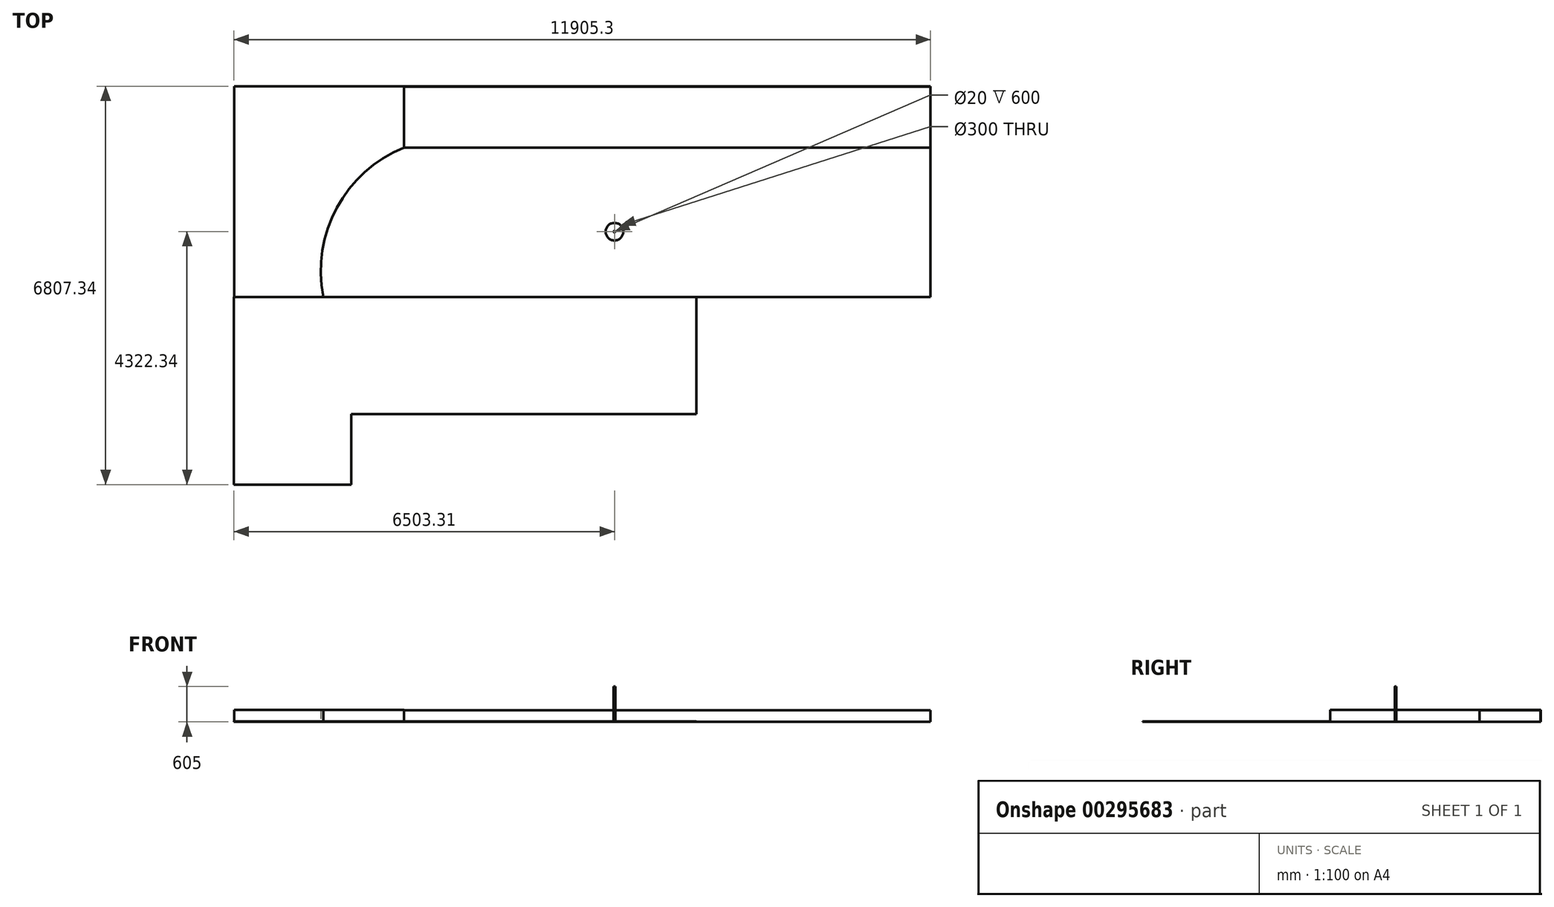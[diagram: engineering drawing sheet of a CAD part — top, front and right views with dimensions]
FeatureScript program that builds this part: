
annotation { "Feature Type Name" : "Feature", "Feature Type Description" : "" }
export const myFeature = defineFeature(function(context is Context, id is Id, definition is map)
    precondition{}
    {
        {
            var Q0;
            Q0=qCreatedBy(makeId("Top.planeOp"),FACE);
            var sketch = newSketch(context, id + "F0", { "sketchPlane" : qUnion([Q0])});
            skLineSegment(sketch, "E0", {"start": v(0, 0) * mm, "end": v(0, 3600) * mm});
            skLineSegment(sketch, "E1", {"start": v(0, 3600) * mm, "end": v(-11900, 3600) * mm});
            skLineSegment(sketch, "E2", {"start": v(-11900, 3600) * mm, "end": v(-11900, -3200) * mm});
            skLineSegment(sketch, "E3", {"start": v(-11900, -3200) * mm, "end": v(-9900, -3200) * mm});
            skLineSegment(sketch, "E4", {"start": v(-9900, -3200) * mm, "end": v(-9900, -2000) * mm});
            skLineSegment(sketch, "E5", {"start": v(-9900, -2000) * mm, "end": v(-9900, 0) * mm});
            skLineSegment(sketch, "E6", {"start": v(-9900, 0) * mm, "end": v(0, 0) * mm});
            skLineSegment(sketch, "E7", {"start": v(-9900, -2000) * mm, "end": v(-4000, -2000) * mm});
            skLineSegment(sketch, "E8", {"start": v(-4000, -2000) * mm, "end": v(-4000, 0) * mm});
            skSolve(sketch);
        }
        {
            var Q0;
            {var subQ0=sQuery(id+"F0.wireOp",EDGE,"E0");Q0=makeQuery(id+"F0.imprint","IMPRINT",FACE,{"disambiguationData":[TD([[makeQuery(id+"F0.imprint","IMPRINT",EDGE,{"derivedFrom":subQ0}),1.0]])]});}
            extrude(context, id + "F1", {"entities" : qUnion([Q0]), "depth" : 5 * mm});
        }
        {
            var Q0;
            Q0=qCreatedBy(makeId("Top.planeOp"),FACE);
            var sketch = newSketch(context, id + "F2", { "sketchPlane" : qUnion([Q0])});
            skLineSegment(sketch, "E9.bottom", {"start": v(-9902, 0) * mm, "end": v(-4002, 0) * mm});
            skLineSegment(sketch, "E9.top", {"start": v(-9902, -2000) * mm, "end": v(-4002, -2000) * mm});
            skLineSegment(sketch, "E9.right", {"start": v(-4002, 0) * mm, "end": v(-4002, -2000) * mm});
            skLineSegment(sketch, "E10", {"start": v(-9902, 0) * mm, "end": v(-11905.3, 0) * mm});
            skLineSegment(sketch, "E11", {"start": v(-11905.3, 0) * mm, "end": v(-11905.3, -3207.34) * mm});
            skLineSegment(sketch, "E12", {"start": v(-11905.3, -3207.34) * mm, "end": v(-9902, -3207.34) * mm});
            skLineSegment(sketch, "E13", {"start": v(-9902, -3207.34) * mm, "end": v(-9902, -2000) * mm});
            skSolve(sketch);
        }
        {
            var Q0;
            Q0 = qSketchRegion(id + "F2", true);
            extrude(context, id + "F3", {"entities" : qUnion([Q0]), "operationType" : NewBodyOperationType.ADD, "depth" : 10 * mm});
        }
        {
            var Q0;
            Q0=qCreatedBy(makeId("Top.planeOp"),FACE);
            var sketch = newSketch(context, id + "F4", { "sketchPlane" : qUnion([Q0])});
            skLineSegment(sketch, "E14.bottom", {"start": v(0, 3592.64) * mm, "end": v(-9000, 3592.64) * mm});
            skLineSegment(sketch, "E14.top", {"start": v(0, 2552.64) * mm, "end": v(-9000, 2552.64) * mm});
            skLineSegment(sketch, "E14.left", {"start": v(0, 3592.64) * mm, "end": v(0, 2552.64) * mm});
            skLineSegment(sketch, "E14.right", {"start": v(-9000, 3592.64) * mm, "end": v(-9000, 2552.64) * mm});
            skSolve(sketch);
        }
        {
            var Q0;
            Q0 = qSketchRegion(id + "F4", true);
            extrude(context, id + "F5", {"entities" : qUnion([Q0]), "operationType" : NewBodyOperationType.ADD, "depth" : 200 * mm});
        }
        {
            var Q0;
            {var subQ0=sQuery(id+"F0.wireOp",EDGE,"E6");var subQ1=sQuery(id+"F0.wireOp",EDGE,"E2");var subQ2=sQuery(id+"F0.wireOp",EDGE,"E1");var subQ3=sQuery(id+"F0.wireOp",EDGE,"E0");Q0=makeQuery(id+"F3.boolean.opBoolean","SPLIT",FACE,{"disambiguationData":[TD([makeQuery(id+"F1.opExtrude","SWEPT_FACE",FACE,{"disambiguationData":[OSD([subQ3])]})])],"derivedFrom":makeQuery(id+"F1.opExtrude","CAP_FACE",FACE,{"disambiguationData":[OSD([subQ3,subQ2,subQ1,sQuery(id+"F0.wireOp",EDGE,"E3"),sQuery(id+"F0.wireOp",EDGE,"E4"),sQuery(id+"F0.wireOp",EDGE,"E5"),subQ0])],"isStart":false})});}
            var sketch = newSketch(context, id + "F6", { "sketchPlane" : qUnion([Q0])});
            skLineSegment(sketch, "E15.bottom", {"start": v(-4002, 0) * mm, "end": v(-5402, 0) * mm});
            skLineSegment(sketch, "E15.top", {"start": v(-4002, 1115) * mm, "end": v(-5402, 1115) * mm});
            skLineSegment(sketch, "E15.left", {"start": v(-4002, 0) * mm, "end": v(-4002, 1115) * mm});
            skLineSegment(sketch, "E15.right", {"start": v(-5402, 0) * mm, "end": v(-5402, 1115) * mm});
            skSolve(sketch);
        }
        {
            var Q0;
            Q0=sQuery(id+"F6.wireOp",VERTEX,"E15.right.end");
            var Q1;
            Q1=makeQuery(id+"F1.opExtrude","SWEPT_BODY",BODY,{"disambiguationData":[OSD([sQuery(id+"F0.wireOp",EDGE,"E0"),sQuery(id+"F0.wireOp",EDGE,"E1"),sQuery(id+"F0.wireOp",EDGE,"E2"),sQuery(id+"F0.wireOp",EDGE,"E3"),sQuery(id+"F0.wireOp",EDGE,"E4"),sQuery(id+"F0.wireOp",EDGE,"E5"),sQuery(id+"F0.wireOp",EDGE,"E6")])]});
            hole(context, id + "F7", {"style" : HoleStyle.SIMPLE, "endStyle" : HoleEndStyle.THROUGH, "holeDiameter" : 300 * mm, "tappedDepth" : 12 * mm, "tapClearance" : 3, "locations" : qUnion([Q0]), "scope" : qUnion([Q1])});
        }
        {
            var Q0;
            {var subQ0=sQuery(id+"F0.wireOp",EDGE,"E6");var subQ1=sQuery(id+"F0.wireOp",EDGE,"E2");var subQ2=sQuery(id+"F0.wireOp",EDGE,"E1");var subQ3=sQuery(id+"F0.wireOp",EDGE,"E0");Q0=makeQuery(id+"F3.boolean.opBoolean","SPLIT",FACE,{"disambiguationData":[TD([makeQuery(id+"F1.opExtrude","SWEPT_FACE",FACE,{"disambiguationData":[OSD([subQ3])]})])],"derivedFrom":makeQuery(id+"F1.opExtrude","CAP_FACE",FACE,{"disambiguationData":[OSD([subQ3,subQ2,subQ1,sQuery(id+"F0.wireOp",EDGE,"E3"),sQuery(id+"F0.wireOp",EDGE,"E4"),sQuery(id+"F0.wireOp",EDGE,"E5"),subQ0])],"isStart":false})});}
            var sketch = newSketch(context, id + "F8", { "sketchPlane" : qUnion([Q0])});
            skLineSegment(sketch, "E16.right", {"start": v(-5402, 0) * mm, "end": v(-5402, 1115) * mm});
            skCircle(sketch, "E17", {"center": v(-5402, 1115) * mm, "radius": 10 * mm});
            skCircle(sketch, "E18", {"center": v(-5402, 1115) * mm, "radius": 15 * mm});
            skSolve(sketch);
        }
        {
            var Q0;
            Q0 = qSketchRegion(id + "F8", true);
            extrude(context, id + "F9", {"entities" : qUnion([Q0]), "depth" : 600 * mm});
        }
        {
            var Q0;
            {var subQ0=sQuery(id+"F0.wireOp",EDGE,"E6");var subQ1=sQuery(id+"F0.wireOp",EDGE,"E2");var subQ2=sQuery(id+"F0.wireOp",EDGE,"E1");var subQ3=sQuery(id+"F0.wireOp",EDGE,"E0");Q0=makeQuery(id+"F3.boolean.opBoolean","SPLIT",FACE,{"disambiguationData":[TD([makeQuery(id+"F1.opExtrude","SWEPT_FACE",FACE,{"disambiguationData":[OSD([subQ3])]})])],"derivedFrom":makeQuery(id+"F1.opExtrude","CAP_FACE",FACE,{"disambiguationData":[OSD([subQ3,subQ2,subQ1,sQuery(id+"F0.wireOp",EDGE,"E3"),sQuery(id+"F0.wireOp",EDGE,"E4"),sQuery(id+"F0.wireOp",EDGE,"E5"),subQ0])],"isStart":false})});}
            var sketch = newSketch(context, id + "F10", { "sketchPlane" : qUnion([Q0])});
            skArc(sketch, "E19", {"start": v(-9000, 2552.64) * mm, "mid": v(-10148.37, 1524.1) * mm, "end": v(-10380.33, 0) * mm});
            skLineSegment(sketch, "E20", {"start": v(-10380.33, 0) * mm, "end": v(-11900, 0) * mm});
            skLineSegment(sketch, "E21", {"start": v(-11900, 0) * mm, "end": v(-11900, 3600) * mm});
            skLineSegment(sketch, "E22", {"start": v(-11900, 3600) * mm, "end": v(-9000, 3592.64) * mm});
            skLineSegment(sketch, "E23", {"start": v(-9000, 3592.64) * mm, "end": v(-9000, 2552.64) * mm});
            skSolve(sketch);
        }
        {
            var Q0;
            Q0 = qSketchRegion(id + "F10", true);
            extrude(context, id + "F11", {"entities" : qUnion([Q0]), "operationType" : NewBodyOperationType.ADD, "depth" : 200 * mm});
        }
    });
